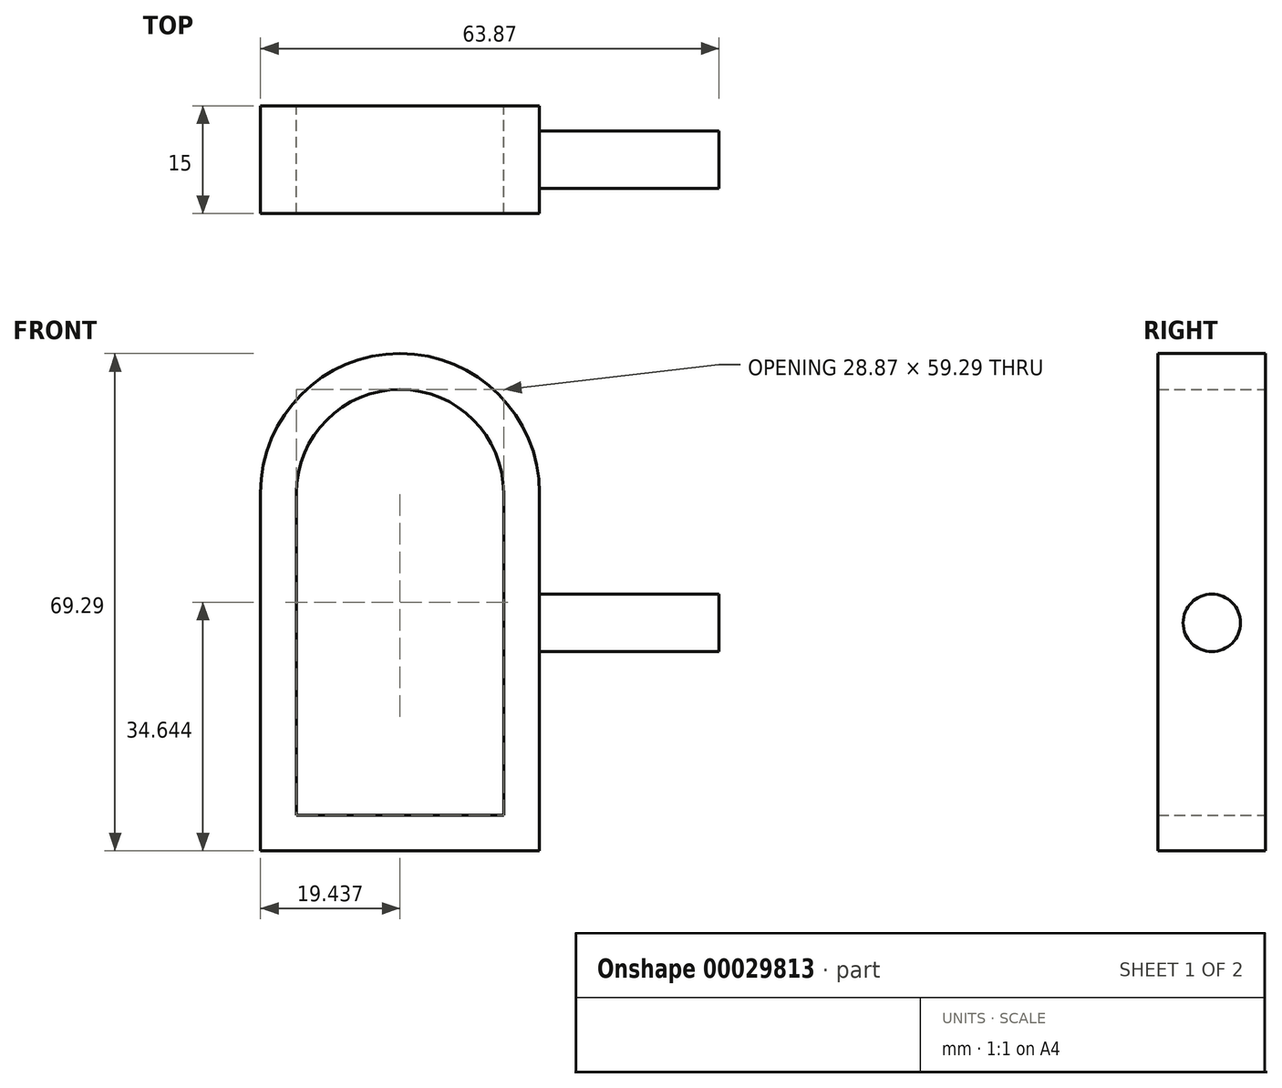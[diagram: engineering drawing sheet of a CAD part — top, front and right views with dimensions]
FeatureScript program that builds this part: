
annotation { "Feature Type Name" : "Feature", "Feature Type Description" : "" }
export const myFeature = defineFeature(function(context is Context, id is Id, definition is map)
    precondition{}
    {
        {
            var Q0;
            Q0=qCreatedBy(makeId("Front.planeOp"),FACE);
            var sketch = newSketch(context, id + "F0", { "sketchPlane" : qUnion([Q0])});
            skLineSegment(sketch, "E0.top", {"start": v(-38.87, 0) * mm, "end": v(0, 0) * mm});
            skLineSegment(sketch, "E0.left", {"start": v(-38.87, 49.85) * mm, "end": v(-38.87, 0) * mm});
            skLineSegment(sketch, "E0.right", {"start": v(0, 49.85) * mm, "end": v(0, 0) * mm});
            skArc(sketch, "E1", {"start": v(0, 49.85) * mm, "mid": v(-19.43, 69.29) * mm, "end": v(-38.87, 49.85) * mm});
            skLineSegment(sketch, "E2.0", {"start": v(-33.87, 49.85) * mm, "end": v(-33.87, 5) * mm});
            skArc(sketch, "E2.1", {"start": v(-5, 49.85) * mm, "mid": v(-19.43, 64.29) * mm, "end": v(-33.87, 49.85) * mm});
            skLineSegment(sketch, "E2.2", {"start": v(-5, 49.85) * mm, "end": v(-5, 5) * mm});
            skLineSegment(sketch, "E2.3", {"start": v(-33.87, 5) * mm, "end": v(-5, 5) * mm});
            skSolve(sketch);
        }
        {
            var Q0;
            Q0=makeQuery(id+"F0.imprint","IMPRINT",FACE,{"disambiguationData":[TD([[makeQuery(id+"F0.imprint","IMPRINT",EDGE,{"derivedFrom":sQuery(id+"F0.wireOp",EDGE,"E0.top")}),1.0]])]});
            extrude(context, id + "F1", {"entities" : qUnion([Q0]), "depth" : 15 * mm});
        }
        {
            var Q0;
            Q0=makeQuery(id+"F1.opExtrude","SWEPT_FACE",FACE,{"disambiguationData":[OSD([sQuery(id+"F0.wireOp",EDGE,"E0.right")])]});
            var sketch = newSketch(context, id + "F2", { "sketchPlane" : qUnion([Q0])});
            skCircle(sketch, "E3", {"center": v(-7.5, 31.77) * mm, "radius": 4 * mm});
            skSolve(sketch);
        }
        {
            var Q0;
            Q0=makeQuery(id+"F2.imprint","IMPRINT",FACE,{"disambiguationData":[TD([[makeQuery(id+"F2.imprint","IMPRINT",EDGE,{"derivedFrom":sQuery(id+"F2.wireOp",EDGE,"E3")}),1.0]])]});
            extrude(context, id + "F3", {"entities" : qUnion([Q0]), "operationType" : NewBodyOperationType.ADD, "depth" : 25 * mm});
        }
    });
